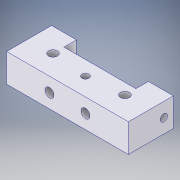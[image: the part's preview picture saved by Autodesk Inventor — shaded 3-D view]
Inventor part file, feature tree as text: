
AUTODESK INVENTOR PART (.ipt)
format: ipt  version: 2017 (Build 210142000, 142)  size: 184,832 bytes
history: native  units: in
note: dims shown in document units (in); Inventor stores cm internally (conversion verified against a paired STEP export)
features: extrude x8, sketch x8, projected_geometry x5
ambient origin geometry x8: Origin, YZ Plane, XZ Plane, XY Plane, X Axis, Y Axis, Z Axis, Center Point
bodies: Solid1 (feature_tree)
feature tree (21):
  extrude  "Extrusion1"  Depth=1.6929in
  extrude  "Extrusion2"  Depth=0.3937in
  extrude  "Extrusion3"  Depth=0.1969in TaperAngle=0.0deg
  extrude  "Extrusion4"  Depth=0.1969in
  extrude  "Extrusion5"  Depth=0.0984in
  extrude  "Extrusion6"  Depth=0.3937in TaperAngle=0.0deg
  extrude  "Extrusion7"  Depth=1.0in
  extrude  "Extrusion8"  Depth=0.625in
  sketch  "Sketch1"  dims[d0=2.4016in d1=1.6929in]
  sketch  "Sketch2"  dims[d2=0.3937in d3=0.0in d4=0.4921in]
  sketch  "Sketch3"  dims[d5=0.0984in d6=0.1969in d7=0.0in]
  projected_geometry  "Projected Loop1"
  sketch  "Sketch4"  dims[d8=0.1969in d9=0.0in d10=0.25in]
  sketch  "Sketch5"  dims[d11=0.25in d12=0.0984in]
  projected_geometry  "Projected Loop2"
  sketch  "Sketch6"  dims[d13=0.0984in d14=0.3937in d15=0.0in]
  projected_geometry  "Projected Loop3"
  sketch  "Sketch7"  dims[d16=1.0in d17=1.5in]
  projected_geometry  "Projected Loop4"
  sketch  "Sketch8"  dims[d18=0.3937in d19=0.0in d20=0.625in d21=1.0in d22=0.0in d23=0.5in d24=0.298in d25=0.125in d26=1.0in d27=0.0in d28=0.25in d29=0.125in d30=0.25in d31=0.125in d32=0.125in d33=0.0in]
  projected_geometry  "Projected Loop5"
